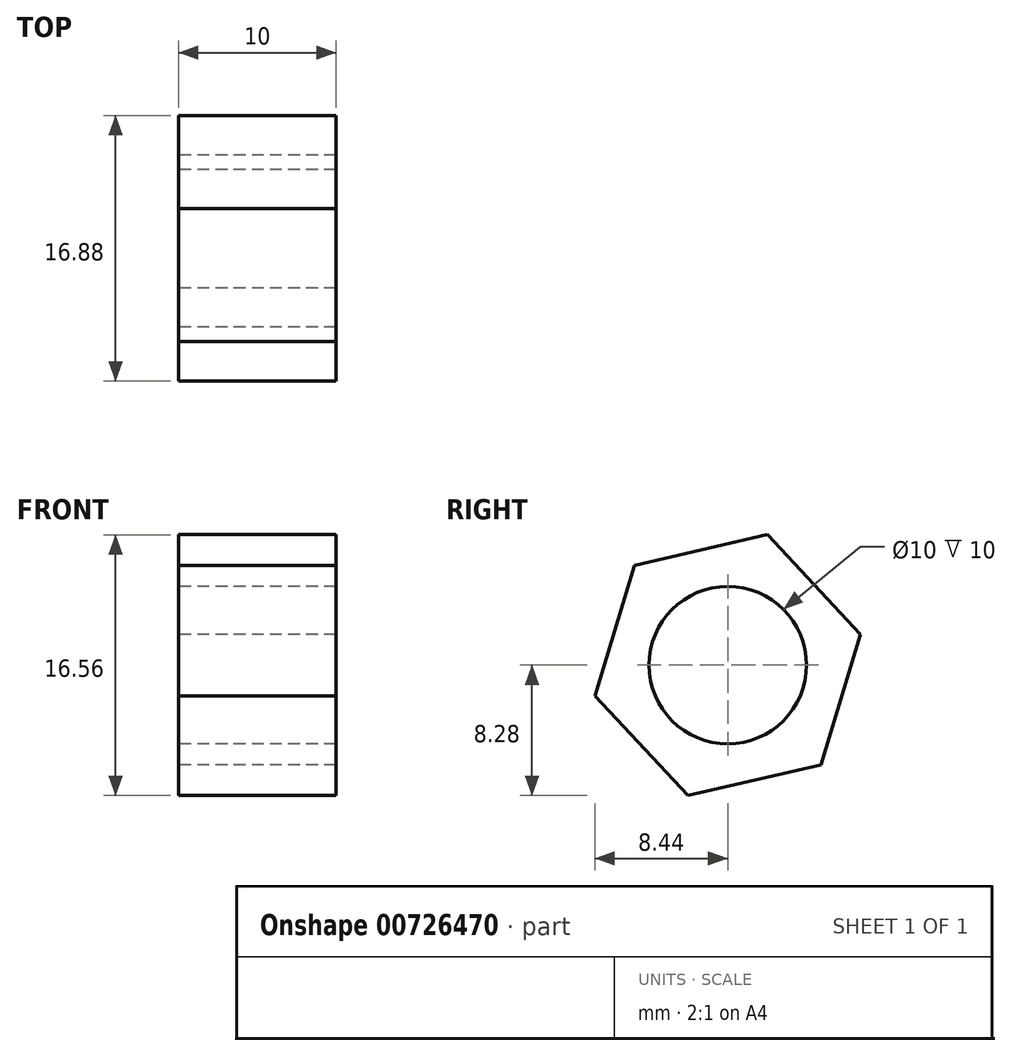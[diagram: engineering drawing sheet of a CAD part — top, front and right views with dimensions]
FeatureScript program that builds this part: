
annotation { "Feature Type Name" : "Feature", "Feature Type Description" : "" }
export const myFeature = defineFeature(function(context is Context, id is Id, definition is map)
    precondition{}
    {
        {
            var Q0;
            Q0=qCreatedBy(makeId("Right.planeOp"),FACE);
            var sketch = newSketch(context, id + "F0", { "sketchPlane" : qUnion([Q0])});
            skCircle(sketch, "E0.cCircle", {"center": v(0, 0) * mm, "radius": 7.5 * mm, "construction": true});
            skLineSegment(sketch, "E0.0", {"start": v(8.44, 1.96) * mm, "end": v(5.91, -6.33) * mm});
            skLineSegment(sketch, "E0.1", {"start": v(5.91, -6.33) * mm, "end": v(-2.52, -8.28) * mm});
            skLineSegment(sketch, "E0.2", {"start": v(-2.52, -8.28) * mm, "end": v(-8.44, -1.96) * mm});
            skLineSegment(sketch, "E0.3", {"start": v(-8.44, -1.96) * mm, "end": v(-5.91, 6.33) * mm});
            skLineSegment(sketch, "E0.4", {"start": v(-5.91, 6.33) * mm, "end": v(2.52, 8.28) * mm});
            skLineSegment(sketch, "E0.5", {"start": v(2.52, 8.28) * mm, "end": v(8.44, 1.96) * mm});
            skPoint(sketch, "E0.0.midPoint", {"position": v(7.17, -2.18) * mm});
            skCircle(sketch, "E1", {"center": v(0, 0) * mm, "radius": 5 * mm});
            skSolve(sketch);
        }
        {
            var Q0;
            Q0=makeQuery(id+"F0.imprint","IMPRINT",FACE,{"disambiguationData":[TD([[makeQuery(id+"F0.imprint","IMPRINT",EDGE,{"derivedFrom":sQuery(id+"F0.wireOp",EDGE,"E0.0")}),-1.0]])]});
            extrude(context, id + "F1", {"entities" : qUnion([Q0]), "depth" : 10 * mm, "offsetDistance" : 25 * mm});
        }
    });
